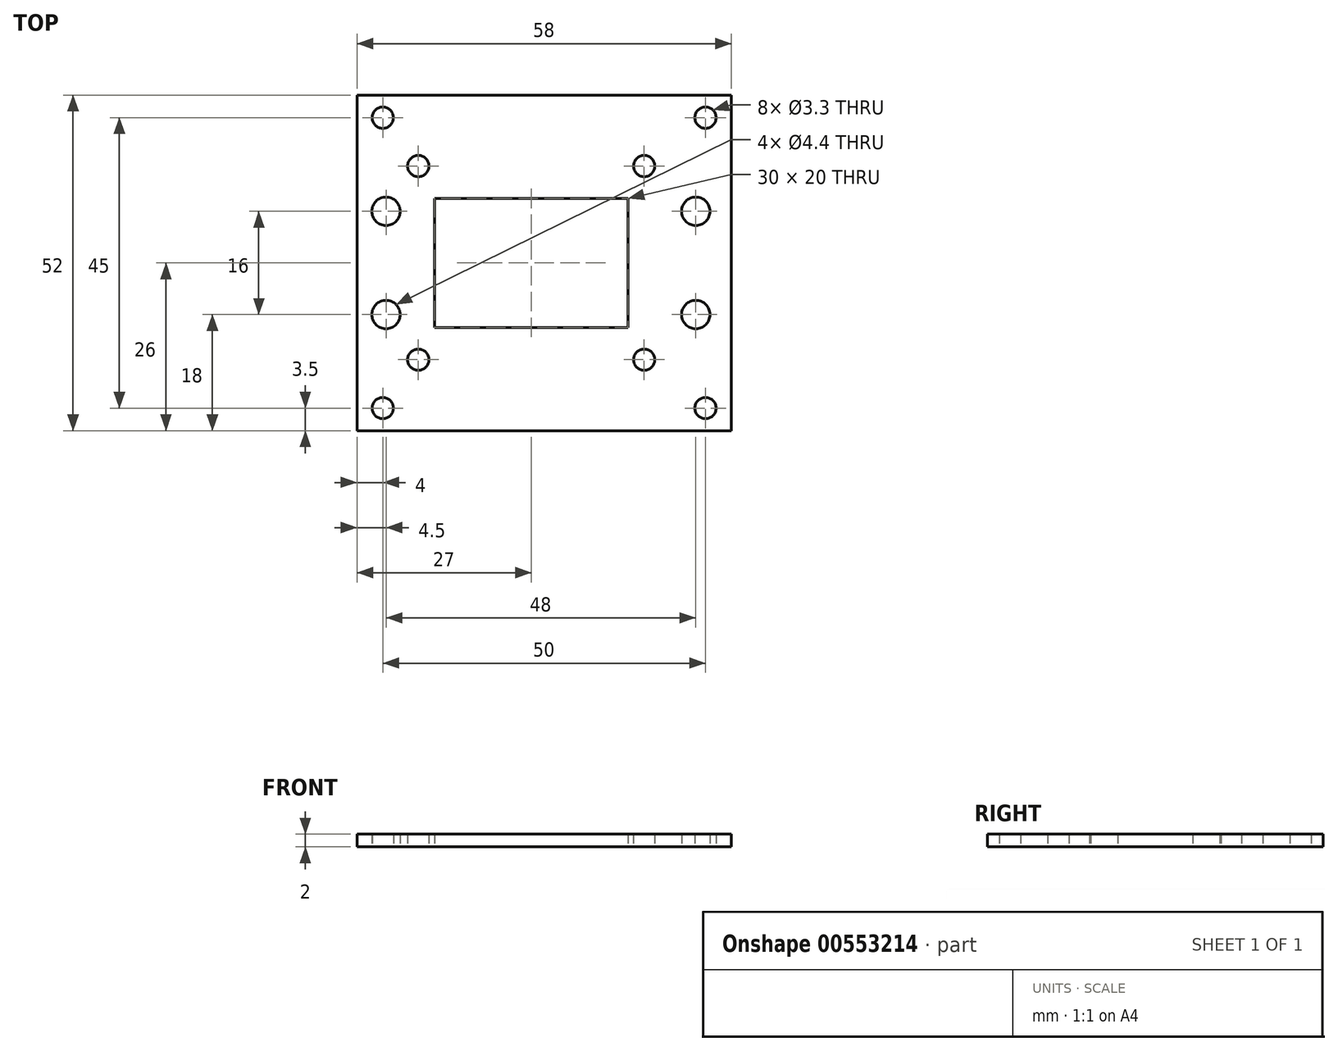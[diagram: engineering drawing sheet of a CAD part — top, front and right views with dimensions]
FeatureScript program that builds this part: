
annotation { "Feature Type Name" : "Feature", "Feature Type Description" : "" }
export const myFeature = defineFeature(function(context is Context, id is Id, definition is map)
    precondition{}
    {
        {
            var Q0;
            Q0=qCreatedBy(makeId("Top.planeOp"),FACE);
            var sketch = newSketch(context, id + "F0", { "sketchPlane" : qUnion([Q0])});
            skLineSegment(sketch, "E0.bottom", {"start": v(-29, 26) * mm, "end": v(29, 26) * mm});
            skLineSegment(sketch, "E0.top", {"start": v(-29, -26) * mm, "end": v(29, -26) * mm});
            skLineSegment(sketch, "E0.right", {"start": v(29, 26) * mm, "end": v(29, -26) * mm});
            skPoint(sketch, "E1", {"position": v(-25, 22.5) * mm});
            skPoint(sketch, "E2", {"position": v(-25, -22.5) * mm});
            skPoint(sketch, "E3", {"position": v(25, -22.5) * mm});
            skPoint(sketch, "E4", {"position": v(25, 22.5) * mm});
            skPoint(sketch, "E5", {"position": v(-19.5, -15) * mm});
            skPoint(sketch, "E6", {"position": v(-19.5, 15) * mm});
            skPoint(sketch, "E7", {"position": v(15.5, 15) * mm});
            skPoint(sketch, "E8", {"position": v(15.5, -15) * mm});
            skLineSegment(sketch, "E9", {"start": v(-29, 26) * mm, "end": v(-29, -26) * mm});
            skPoint(sketch, "E10", {"position": v(-24.5, -8) * mm});
            skPoint(sketch, "E11", {"position": v(-24.5, 8) * mm});
            skLineSegment(sketch, "E12.bottom", {"start": v(-17, -10) * mm, "end": v(13, -10) * mm});
            skLineSegment(sketch, "E12.top", {"start": v(-17, 10) * mm, "end": v(13, 10) * mm});
            skLineSegment(sketch, "E12.left", {"start": v(-17, -10) * mm, "end": v(-17, 10) * mm});
            skLineSegment(sketch, "E12.right", {"start": v(13, -10) * mm, "end": v(13, 10) * mm});
            skPoint(sketch, "E13", {"position": v(23.5, -8) * mm});
            skPoint(sketch, "E14", {"position": v(23.5, 8) * mm});
            skSolve(sketch);
        }
        {
            var Q0;
            Q0=makeQuery(id+"F0.imprint","IMPRINT",FACE,{"disambiguationData":[TD([[makeQuery(id+"F0.imprint","IMPRINT",EDGE,{"derivedFrom":sQuery(id+"F0.wireOp",EDGE,"E0.bottom")}),-1.0]])]});
            extrude(context, id + "F1", {"entities" : qUnion([Q0]), "depth" : 2 * mm, "offsetDistance" : 25 * mm});
        }
        {
            var Q0;
            Q0=sQuery(id+"F0.wireOp",VERTEX,"E5");
            var Q1;
            Q1=sQuery(id+"F0.wireOp",VERTEX,"E2");
            var Q2;
            Q2=sQuery(id+"F0.wireOp",VERTEX,"E6");
            var Q3;
            Q3=sQuery(id+"F0.wireOp",VERTEX,"E1");
            var Q4;
            Q4=sQuery(id+"F0.wireOp",VERTEX,"E8");
            var Q5;
            Q5=sQuery(id+"F0.wireOp",VERTEX,"E7");
            var Q6;
            Q6=sQuery(id+"F0.wireOp",VERTEX,"E4");
            var Q7;
            Q7=sQuery(id+"F0.wireOp",VERTEX,"E3");
            var Q8;
            Q8=makeQuery(id+"F1.opExtrude","SWEPT_BODY",BODY,{"disambiguationData":[OSD([sQuery(id+"F0.wireOp",EDGE,"E0.bottom"),sQuery(id+"F0.wireOp",EDGE,"E0.top"),sQuery(id+"F0.wireOp",EDGE,"E0.left"),sQuery(id+"F0.wireOp",EDGE,"E0.right")])]});
            hole(context, id + "F2", {"style" : HoleStyle.SIMPLE, "endStyle" : HoleEndStyle.THROUGH, "oppositeDirection" : true, "standardTappedOrClearance" : lookupTablePath({ "standard" : "ISO", "fit" : "Normal", "size" : "M3", "type" : "Clearance" }), "standardBlindInLast" : lookupTablePath({ "fit" : "Standard", "standard" : "ISO", "size" : "M3", "type" : "Clearance" }), "holeDiameter" : 3.3 * mm, "isTappedThrough" : true, "tappedDepth" : 12 * mm, "tapClearance" : 3, "locations" : qUnion([Q0, Q1, Q2, Q3, Q4, Q5, Q6, Q7]), "scope" : qUnion([Q8])});
        }
        {
            var Q0;
            Q0=sQuery(id+"F0.wireOp",VERTEX,"E10");
            var Q1;
            Q1=sQuery(id+"F0.wireOp",VERTEX,"E11");
            var Q2;
            Q2=sQuery(id+"F0.wireOp",VERTEX,"E13");
            var Q3;
            Q3=sQuery(id+"F0.wireOp",VERTEX,"E14");
            var Q4;
            Q4=makeQuery(id+"F1.opExtrude","SWEPT_BODY",BODY,{"disambiguationData":[OSD([sQuery(id+"F0.wireOp",EDGE,"E0.bottom"),sQuery(id+"F0.wireOp",EDGE,"E0.top"),sQuery(id+"F0.wireOp",EDGE,"E0.left"),sQuery(id+"F0.wireOp",EDGE,"E0.right"),sQuery(id+"F0.wireOp",EDGE,"E9"),sQuery(id+"F0.wireOp",EDGE,"XkV2TfUW-qYEH-QFIG-PaCm-sAAAoikqqGsH.bottom"),sQuery(id+"F0.wireOp",EDGE,"XkV2TfUW-qYEH-QFIG-PaCm-sAAAoikqqGsH.top"),sQuery(id+"F0.wireOp",EDGE,"XkV2TfUW-qYEH-QFIG-PaCm-sAAAoikqqGsH.right"),sQuery(id+"F0.wireOp",EDGE,"E12.bottom"),sQuery(id+"F0.wireOp",EDGE,"E12.top"),sQuery(id+"F0.wireOp",EDGE,"E12.left"),sQuery(id+"F0.wireOp",EDGE,"E12.right")])]});
            hole(context, id + "F3", {"style" : HoleStyle.SIMPLE, "endStyle" : HoleEndStyle.THROUGH, "oppositeDirection" : true, "standardTappedOrClearance" : lookupTablePath({ "standard" : "ISO", "fit" : "Normal", "size" : "M4", "type" : "Clearance" }), "standardBlindInLast" : lookupTablePath({ "fit" : "Standard", "standard" : "ISO", "size" : "M4", "type" : "Clearance" }), "holeDiameter" : 4.4 * mm, "isTappedThrough" : true, "tappedDepth" : 12 * mm, "tapClearance" : 3, "locations" : qUnion([Q0, Q1, Q2, Q3]), "scope" : qUnion([Q4])});
        }
    });
